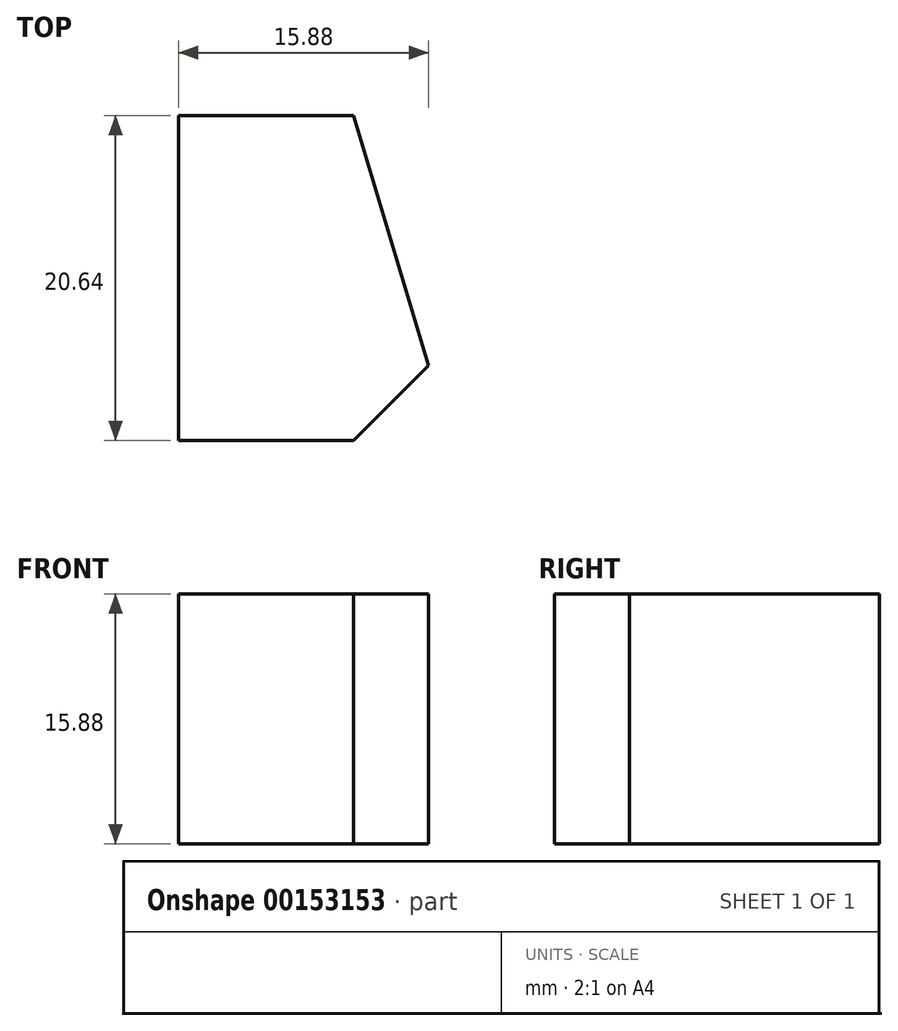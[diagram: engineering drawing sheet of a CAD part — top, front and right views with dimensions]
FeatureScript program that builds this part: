
annotation { "Feature Type Name" : "Feature", "Feature Type Description" : "" }
export const myFeature = defineFeature(function(context is Context, id is Id, definition is map)
    precondition{}
    {
        {
            var Q0;
            Q0=qCreatedBy(makeId("Top.planeOp"),FACE);
            var sketch = newSketch(context, id + "F0", { "sketchPlane" : qUnion([Q0])});
            skLineSegment(sketch, "E0.rect.bottom", {"start": v(7.94, -7.94) * mm, "end": v(-7.94, -7.94) * mm});
            skLineSegment(sketch, "E0.rect.top", {"start": v(7.94, 7.94) * mm, "end": v(-7.94, 7.94) * mm});
            skLineSegment(sketch, "E0.rect.left", {"start": v(7.94, -7.94) * mm, "end": v(7.94, 7.94) * mm});
            skLineSegment(sketch, "E0.rect.right", {"start": v(-7.94, -7.94) * mm, "end": v(-7.94, 7.94) * mm});
            skPoint(sketch, "E0.rect.middle", {"position": v(0, 0) * mm});
            skSolve(sketch);
        }
        {
            var Q0;
            Q0=qSketchRegion(id+"F0",true);
            extrude(context, id + "F1", {"entities" : qUnion([Q0]), "oppositeDirection" : true, "depth" : 20.64 * mm});
        }
        {
            var Q0;
            Q0=makeQuery(id+"F1.opExtrude","SWEPT_FACE",FACE,{"disambiguationData":[OSD([sQuery(id+"F0.wireOp",EDGE,"E0.rect.bottom")])]});
            var sketch = newSketch(context, id + "F2", { "sketchPlane" : qUnion([Q0])});
            skLineSegment(sketch, "E1", {"start": v(3.17, 0) * mm, "end": v(7.94, -15.88) * mm});
            skLineSegment(sketch, "E2", {"start": v(7.94, -15.88) * mm, "end": v(7.94, 0) * mm});
            skLineSegment(sketch, "E3", {"start": v(7.94, 0) * mm, "end": v(3.17, 0) * mm});
            skSolve(sketch);
        }
        {
            var Q0;
            Q0=qSketchRegion(id+"F2",true);
            extrude(context, id + "F3", {"entities" : qUnion([Q0]), "operationType" : NewBodyOperationType.REMOVE, "endBound" : BoundingType.THROUGH_ALL, "oppositeDirection" : true, "depth" : 25.4 * mm});
        }
        {
            var Q0;
            Q0=makeQuery(id+"F1.opExtrude","SWEPT_FACE",FACE,{"disambiguationData":[OSD([sQuery(id+"F0.wireOp",EDGE,"E0.rect.bottom")])]});
            var sketch = newSketch(context, id + "F4", { "sketchPlane" : qUnion([Q0])});
            skLineSegment(sketch, "E4", {"start": v(7.94, -15.88) * mm, "end": v(3.17, -20.64) * mm});
            skLineSegment(sketch, "E5", {"start": v(3.17, -20.64) * mm, "end": v(7.94, -20.64) * mm});
            skLineSegment(sketch, "E6", {"start": v(7.94, -20.64) * mm, "end": v(7.94, -15.88) * mm});
            skSolve(sketch);
        }
        {
            var Q0;
            Q0=qSketchRegion(id+"F4",true);
            extrude(context, id + "F5", {"entities" : qUnion([Q0]), "operationType" : NewBodyOperationType.REMOVE, "endBound" : BoundingType.THROUGH_ALL, "oppositeDirection" : true, "depth" : 25.4 * mm});
        }
        {
            var Q0;
            Q0=makeQuery(id+"F1.opExtrude","SWEPT_BODY",BODY,{"disambiguationData":[OSD([sQuery(id+"F0.wireOp",EDGE,"E0.rect.bottom"),sQuery(id+"F0.wireOp",EDGE,"E0.rect.top"),sQuery(id+"F0.wireOp",EDGE,"E0.rect.left"),sQuery(id+"F0.wireOp",EDGE,"E0.rect.right")])]});
            var Q1;
            {var subQ0=sQuery(id+"F0.wireOp",EDGE,"E0.rect.bottom");var subQ1=sQuery(id+"F0.wireOp",EDGE,"E0.rect.left");Q1=makeQuery(id+"F8fKRqUSVpU3u6o_1.boolean.opBoolean","SPLIT",EDGE,{"disambiguationData":[TD([makeQuery(id+"F1.opExtrude","SWEPT_FACE",FACE,{"disambiguationData":[OSD([subQ1])]})])],"derivedFrom":makeQuery(id+"F1.opExtrude","CAP_EDGE",EDGE,{"disambiguationData":[OSD([subQ0])],"isStart":true})});}
            transform(context, id + "F6", {"entities" : qUnion([Q0]), "transformType" : TransformType.TRANSLATION_DISTANCE, "transformDirection" : qUnion([Q1]), "distance" : 7.94 * mm, "makeCopy" : false});
        }
        {
            var Q0;
            Q0=makeQuery(id+"F1.opExtrude","SWEPT_BODY",BODY,{"disambiguationData":[OSD([sQuery(id+"F0.wireOp",EDGE,"E0.rect.bottom"),sQuery(id+"F0.wireOp",EDGE,"E0.rect.top"),sQuery(id+"F0.wireOp",EDGE,"E0.rect.left"),sQuery(id+"F0.wireOp",EDGE,"E0.rect.right")])]});
            var Q1;
            Q1=makeQuery(id+"F1.opExtrude","CAP_EDGE",EDGE,{"disambiguationData":[OSD([sQuery(id+"F0.wireOp",EDGE,"E0.rect.right")])],"isStart":true});
            transform(context, id + "F7", {"entities" : qUnion([Q0]), "transformType" : TransformType.TRANSLATION_DISTANCE, "transformDirection" : qUnion([Q1]), "distance" : 7.94 * mm, "makeCopy" : false});
        }
        {
            var Q0;
            Q0=makeQuery(id+"F1.opExtrude","SWEPT_BODY",BODY,{"disambiguationData":[OSD([sQuery(id+"F0.wireOp",EDGE,"E0.rect.bottom"),sQuery(id+"F0.wireOp",EDGE,"E0.rect.top"),sQuery(id+"F0.wireOp",EDGE,"E0.rect.left"),sQuery(id+"F0.wireOp",EDGE,"E0.rect.right")])]});
            var Q1;
            Q1=makeQuery(id+"F1.opExtrude","CAP_EDGE",EDGE,{"disambiguationData":[OSD([sQuery(id+"F0.wireOp",EDGE,"E0.rect.bottom")])],"isStart":true});
            transform(context, id + "F8", {"entities" : qUnion([Q0]), "transformType" : TransformType.ROTATION, "transformAxis" : qUnion([Q1]), "angle" : 90 * degree, "makeCopy" : false});
        }
    });
